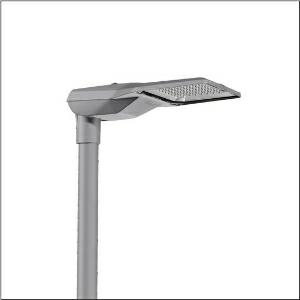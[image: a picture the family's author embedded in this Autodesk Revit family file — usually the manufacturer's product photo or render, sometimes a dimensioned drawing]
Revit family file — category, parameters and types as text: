
# Revit family: streetlight_sl_21_midi___pl52_5xe3h43s08lb_5466
name_source: partatom
category: Lighting Fixtures
units: mm (PartAtom-declared; Revit-internal decimal feet)

## family parameters
Cut with Voids When Loaded = No
Host = Face
Light Source = No
Part Type = Normal
Room Calculation Point = No
Round Connector Dimension = Use Diameter
Shared = No

## types (1)
- --- (1 x LED, 14690 lm, 99.6 W, 4000K)
    Apparent Load = 100 VA
    CIE Flux Codes = 27 59 98 100 100
    Color Rendering = 70
    Color Temperature = 4000K
    Default Elevation = 1800 mm
    Description = Streetlight SL 21 midi, mast luminaire, primary light control with lens, of PMMA, primary optical cover: cover, of toughened safety glass, transparent, light distribution: PL52, light emission: direct distribution, primary light characteristic: asymmetric, installation type: side-entry, post-top, LED, High Power LED, rated luminous flux: 14.690lm, luminous efficacy: 148lm/W, light colour: 740, colour temperature: 4000K, control gear: D4i, control: overheat protection, constant luminous flux control, time-dependent luminous flux control, flexible luminous flux parameterisation, pre-setting: logarithmic dimming characteristic, mains connection: 230..240V, AC, 50/60Hz, start of lifetime: 100W, end of service life: 102W, reduction: 46W, luminaire housing, of diecast aluminium, powder-coated, Siteco® metallic grey (DB 702S), corrosivity category C5 mid according to DIN EN ISO 12944, please order mast flange separately, inclination adjustable: 0°, 5°, 10°, 15°, sealing non-destructively replaceable, multi-level sealing system, length: 644mm, width: 335mm, height: 110mm, mast flange for spigot size: 42mm (side-entry): 5XC10008XM4, 60/48mm (side-entry/post-top): 5XC10108XM2, 76/60mm (side-entry/post-top): 5XC10108XM1, mounting height: 4..8m, Smart Interface above, protection rating (complete): IP66, insulation class (complete): insulation class II (safety insulation), certification: CE, ENEC, ENEC+, VDE, impact resistance: IK10, permissible operating ambient temperature for outdoor applications: -40..+50°C, standard-compliant lighting for roads and squares, packaging unit: 1 piece

Light Distribution: PL52
    Height = 111 mm
    Lamp = 1 x LED
    Lamp Light Flux = 14690 lm
    Lamp Power = 99.6 W
    Lamp count = 1
    Length = 644 mm
    Luminous efficacy = 147 lm/W
    Manufacturer = Siteco
    ModVariant = No
    Model = 5XE3H43S08LB
    Number of Poles = 1
    OnlyDefault = Yes
    Power Factor = 1
    Product Name = Streetlight SL 21 midi | PL52
    Product group = mast luminaire | pylon top
    ProductGroupID = 6100
    Protection Class = Protection class II
    Protection Degree = IP 66
    RLX_Detail_Level = 1
    RLX_Emergency_Light_Flux = 0 lm
    RLX_Emergency_Type = 0
    RLX_Emergency_Type_DB = No
    RlxData = <blob elided: 36389 chars, md5=9eb848d0>
    Socket = socket
    Standby Power = 0 W
    System Light Flux = 14690 lm
    System Power = 100 W
    Type Comments = factory setting: luminous flux: 100 % | dim-lin: 254 | 1020 mA
    Type Image = l_1004302.jpg
    URL = http://relux.com
    VarID = @adj_012517
    Voltage = 0 V
    Weight = 0.00 kg
    Width = 336 mm

## geometry (parser evidence)
native form markers: Blend x4, Sweep x11
no freeform markers — native parametric forms only
